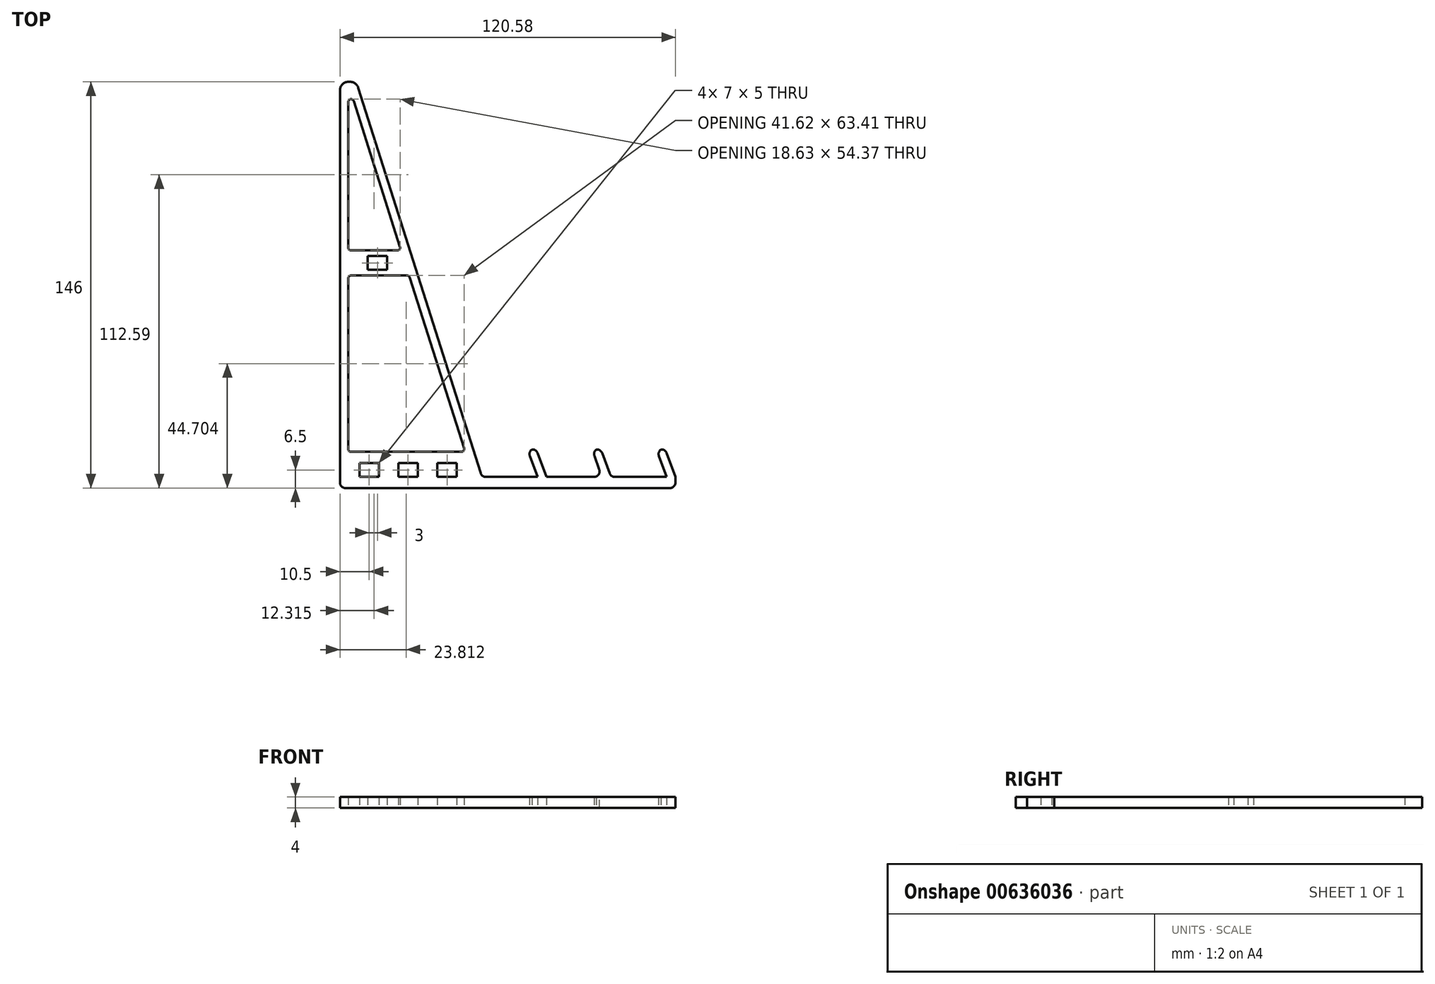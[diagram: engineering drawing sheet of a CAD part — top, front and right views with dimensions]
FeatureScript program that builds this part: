
annotation { "Feature Type Name" : "Feature", "Feature Type Description" : "" }
export const myFeature = defineFeature(function(context is Context, id is Id, definition is map)
    precondition{}
    {
        {
            var Q0;
            Q0=qCreatedBy(makeId("Top.planeOp"),FACE);
            var sketch = newSketch(context, id + "F0", { "sketchPlane" : qUnion([Q0])});
            skLineSegment(sketch, "E0", {"start": v(-51, -4) * mm, "end": v(-51, 139) * mm});
            skLineSegment(sketch, "E1.bottom", {"start": v(-44, 5) * mm, "end": v(-37, 5) * mm});
            skLineSegment(sketch, "E1.top", {"start": v(-44, 0) * mm, "end": v(-37, 0) * mm});
            skLineSegment(sketch, "E1.left", {"start": v(-44, 5) * mm, "end": v(-44, 0) * mm});
            skLineSegment(sketch, "E1.right", {"start": v(-37, 5) * mm, "end": v(-37, 0) * mm});
            skLineSegment(sketch, "E2", {"start": v(-44.43, 139.9) * mm, "end": v(0, 0) * mm});
            skLineSegment(sketch, "E3", {"start": v(-46.05, 135.09) * mm, "end": v(-29.41, 82.71) * mm});
            skLineSegment(sketch, "E4", {"start": v(-30.37, 81.4) * mm, "end": v(-47, 81.4) * mm});
            skLineSegment(sketch, "E5", {"start": v(-48, 82.4) * mm, "end": v(-48, 134.78) * mm});
            skLineSegment(sketch, "E6", {"start": v(-47, 9) * mm, "end": v(-7.37, 9) * mm});
            skLineSegment(sketch, "E7", {"start": v(-6.42, 10.3) * mm, "end": v(-25.92, 71.71) * mm});
            skLineSegment(sketch, "E8", {"start": v(-26.87, 72.4) * mm, "end": v(-47, 72.4) * mm});
            skLineSegment(sketch, "E9", {"start": v(-48, 71.4) * mm, "end": v(-48, 10) * mm});
            skPoint(sketch, "E10.visualSharp", {"position": v(-48, 141.24) * mm});
            skArc(sketch, "E10.filletArc", {"start": v(-46.05, 135.09) * mm, "mid": v(-47.15, 135.77) * mm, "end": v(-48, 134.78) * mm});
            skPoint(sketch, "E11.visualSharp", {"position": v(-48, 81.4) * mm});
            skArc(sketch, "E11.filletArc", {"start": v(-48, 82.4) * mm, "mid": v(-47.7, 81.7) * mm, "end": v(-47, 81.4) * mm});
            skPoint(sketch, "E12.visualSharp", {"position": v(-29, 81.4) * mm});
            skArc(sketch, "E12.filletArc", {"start": v(-30.37, 81.4) * mm, "mid": v(-29.56, 81.82) * mm, "end": v(-29.41, 82.71) * mm});
            skPoint(sketch, "E13.visualSharp", {"position": v(-26.14, 72.4) * mm});
            skArc(sketch, "E13.filletArc", {"start": v(-25.92, 71.71) * mm, "mid": v(-26.28, 72.21) * mm, "end": v(-26.87, 72.4) * mm});
            skPoint(sketch, "E14.visualSharp", {"position": v(-48, 72.4) * mm});
            skArc(sketch, "E14.filletArc", {"start": v(-47, 72.4) * mm, "mid": v(-47.7, 72.11) * mm, "end": v(-48, 71.4) * mm});
            skPoint(sketch, "E15.visualSharp", {"position": v(-48, 9) * mm});
            skArc(sketch, "E15.filletArc", {"start": v(-48, 10) * mm, "mid": v(-47.7, 9.3) * mm, "end": v(-47, 9) * mm});
            skPoint(sketch, "E16.visualSharp", {"position": v(-6, 9) * mm});
            skArc(sketch, "E16.filletArc", {"start": v(-7.37, 9) * mm, "mid": v(-6.57, 9.4) * mm, "end": v(-6.42, 10.3) * mm});
            skLineSegment(sketch, "E17.1.0.0", {"start": v(-30, 5) * mm, "end": v(-23, 5) * mm});
            skLineSegment(sketch, "E17.1.0.1", {"start": v(-23, 5) * mm, "end": v(-23, 0) * mm});
            skLineSegment(sketch, "E17.1.0.2", {"start": v(-30, 0) * mm, "end": v(-23, 0) * mm});
            skLineSegment(sketch, "E17.1.0.3", {"start": v(-30, 5) * mm, "end": v(-30, 0) * mm});
            skLineSegment(sketch, "E17.2.0.0", {"start": v(-16, 5) * mm, "end": v(-9, 5) * mm});
            skLineSegment(sketch, "E17.2.0.1", {"start": v(-9, 5) * mm, "end": v(-9, 0) * mm});
            skLineSegment(sketch, "E17.2.0.2", {"start": v(-16, 0) * mm, "end": v(-9, 0) * mm});
            skLineSegment(sketch, "E17.2.0.3", {"start": v(-16, 5) * mm, "end": v(-16, 0) * mm});
            skLineSegment(sketch, "E17.direction1", {"start": v(-44, 5) * mm, "end": v(-30, 5) * mm, "construction": true});
            skLineSegment(sketch, "E18.bottom", {"start": v(-41, 79.4) * mm, "end": v(-34, 79.4) * mm});
            skLineSegment(sketch, "E18.top", {"start": v(-41, 74.4) * mm, "end": v(-34, 74.4) * mm});
            skLineSegment(sketch, "E18.left", {"start": v(-41, 79.4) * mm, "end": v(-41, 74.4) * mm});
            skLineSegment(sketch, "E18.right", {"start": v(-34, 79.4) * mm, "end": v(-34, 74.4) * mm});
            skLineSegment(sketch, "E19", {"start": v(-48, 142) * mm, "end": v(-47.29, 142) * mm});
            skPoint(sketch, "E20.visualSharp", {"position": v(-45.1, 142) * mm});
            skArc(sketch, "E20.filletArc", {"start": v(-44.43, 139.9) * mm, "mid": v(-45.52, 141.42) * mm, "end": v(-47.29, 142) * mm});
            skPoint(sketch, "E21.visualSharp", {"position": v(-51, 142) * mm});
            skArc(sketch, "E21.filletArc", {"start": v(-48, 142) * mm, "mid": v(-50.12, 141.12) * mm, "end": v(-51, 139) * mm});
            skLineSegment(sketch, "E22", {"start": v(20, 0) * mm, "end": v(16.58, 9.4) * mm});
            skLineSegment(sketch, "E23", {"start": v(16.58, 9.4) * mm, "end": v(19.4, 10.42) * mm});
            skLineSegment(sketch, "E24", {"start": v(19.4, 10.42) * mm, "end": v(23.2, 0) * mm});
            skLineSegment(sketch, "E25", {"start": v(69.58, 0) * mm, "end": v(65.78, 10.42) * mm});
            skLineSegment(sketch, "E26", {"start": v(65.78, 10.42) * mm, "end": v(62.96, 9.4) * mm});
            skLineSegment(sketch, "E27", {"start": v(62.96, 9.4) * mm, "end": v(66.39, 0) * mm});
            skLineSegment(sketch, "E28", {"start": v(43.2, 0) * mm, "end": v(39.77, 9.4) * mm});
            skLineSegment(sketch, "E29", {"start": v(39.77, 9.4) * mm, "end": v(42.6, 10.42) * mm});
            skLineSegment(sketch, "E30", {"start": v(42.6, 10.42) * mm, "end": v(46.39, 0) * mm});
            skLineSegment(sketch, "E31", {"start": v(46.39, 0) * mm, "end": v(43.2, 0) * mm});
            skLineSegment(sketch, "E32", {"start": v(66.39, 0) * mm, "end": v(69.58, 0) * mm});
            skLineSegment(sketch, "E33", {"start": v(20, 0) * mm, "end": v(23.2, 0) * mm});
            skLineSegment(sketch, "E34", {"start": v(0, 0) * mm, "end": v(69.58, 0) * mm});
            skLineSegment(sketch, "E35", {"start": v(69.58, -4) * mm, "end": v(69.58, 0) * mm});
            skLineSegment(sketch, "E36", {"start": v(-51, -4) * mm, "end": v(69.58, -4) * mm});
            skSolve(sketch);
        }
        {
            var Q0;
            Q0=qSketchRegion(id+"F0",true);
            extrude(context, id + "F1", {"entities" : qUnion([Q0]), "depth" : 4 * mm, "offsetDistance" : 25 * mm});
        }
        {
            var Q0;
            Q0=makeQuery(id+"F1.opExtrude","SWEPT_EDGE",EDGE,{"disambiguationData":[OSD([sQuery(id+"F0.wireOp",EDGE,"gvBwSrxk-zvvE-uQVS-XaT0-VaHBcBpJHqCH"),sQuery(id+"F0.wireOp",EDGE,"E0")])]});
            var Q1;
            Q1=makeQuery(id+"F1.opExtrude","SWEPT_EDGE",EDGE,{"disambiguationData":[OSD([sQuery(id+"F0.wireOp",EDGE,"gvBwSrxk-zvvE-uQVS-XaT0-VaHBcBpJHqCH"),sQuery(id+"F0.wireOp",EDGE,"nh6h67nY-TW2N-W8gg-voCM-LFL465GMrIJx")])]});
            var Q2;
            Q2=makeQuery(id+"F1.opExtrude","SWEPT_EDGE",EDGE,{"disambiguationData":[OSD([sQuery(id+"F0.wireOp",EDGE,"nh6h67nY-TW2N-W8gg-voCM-LFL465GMrIJx"),sQuery(id+"F0.wireOp",EDGE,"E25"),sQuery(id+"F0.wireOp",EDGE,"9GKQQmJT-vaMx-PueB-U0vb-JAIJfWlyNM5I")])]});
            var Q3;
            Q3=makeQuery(id+"F1.opExtrude","SWEPT_EDGE",EDGE,{"disambiguationData":[OSD([sQuery(id+"F0.wireOp",EDGE,"E25"),sQuery(id+"F0.wireOp",EDGE,"E26")])]});
            var Q4;
            Q4=makeQuery(id+"F1.opExtrude","SWEPT_EDGE",EDGE,{"disambiguationData":[OSD([sQuery(id+"F0.wireOp",EDGE,"E26"),sQuery(id+"F0.wireOp",EDGE,"E27")])]});
            var Q5;
            Q5=makeQuery(id+"F1.opExtrude","SWEPT_EDGE",EDGE,{"disambiguationData":[OSD([sQuery(id+"F0.wireOp",EDGE,"UcYIQvCT-M2cl-KZQb-FalE-3mOYIRNoCB6S"),sQuery(id+"F0.wireOp",EDGE,"E27"),sQuery(id+"F0.wireOp",EDGE,"9GKQQmJT-vaMx-PueB-U0vb-JAIJfWlyNM5I")])]});
            var Q6;
            Q6=makeQuery(id+"F1.opExtrude","SWEPT_EDGE",EDGE,{"disambiguationData":[OSD([sQuery(id+"F0.wireOp",EDGE,"E24"),sQuery(id+"F0.wireOp",EDGE,"UcYIQvCT-M2cl-KZQb-FalE-3mOYIRNoCB6S")])]});
            var Q7;
            Q7=makeQuery(id+"F1.opExtrude","SWEPT_EDGE",EDGE,{"disambiguationData":[OSD([sQuery(id+"F0.wireOp",EDGE,"E23"),sQuery(id+"F0.wireOp",EDGE,"E24")])]});
            var Q8;
            Q8=makeQuery(id+"F1.opExtrude","SWEPT_EDGE",EDGE,{"disambiguationData":[OSD([sQuery(id+"F0.wireOp",EDGE,"E22"),sQuery(id+"F0.wireOp",EDGE,"E23")])]});
            var Q9;
            Q9=makeQuery(id+"F1.opExtrude","SWEPT_EDGE",EDGE,{"disambiguationData":[OSD([sQuery(id+"F0.wireOp",EDGE,"E22"),sQuery(id+"F0.wireOp",EDGE,"UcYIQvCT-M2cl-KZQb-FalE-3mOYIRNoCB6S")])]});
            var Q10;
            Q10=makeQuery(id+"F1.opExtrude","SWEPT_EDGE",EDGE,{"disambiguationData":[OSD([sQuery(id+"F0.wireOp",EDGE,"E2"),sQuery(id+"F0.wireOp",EDGE,"UcYIQvCT-M2cl-KZQb-FalE-3mOYIRNoCB6S")])]});
            var Q11;
            Q11=makeQuery(id+"F1.opExtrude","SWEPT_EDGE",EDGE,{"disambiguationData":[OSD([sQuery(id+"F0.wireOp",EDGE,"E28"),sQuery(id+"F0.wireOp",EDGE,"E29")])]});
            var Q12;
            Q12=makeQuery(id+"F1.opExtrude","SWEPT_EDGE",EDGE,{"disambiguationData":[OSD([sQuery(id+"F0.wireOp",EDGE,"E29"),sQuery(id+"F0.wireOp",EDGE,"E30")])]});
            var Q13;
            Q13=makeQuery(id+"F1.opExtrude","SWEPT_EDGE",EDGE,{"disambiguationData":[OSD([sQuery(id+"F0.wireOp",EDGE,"UcYIQvCT-M2cl-KZQb-FalE-3mOYIRNoCB6S"),sQuery(id+"F0.wireOp",EDGE,"E28"),sQuery(id+"F0.wireOp",EDGE,"E31")])]});
            var Q14;
            Q14=makeQuery(id+"F1.opExtrude","SWEPT_EDGE",EDGE,{"disambiguationData":[OSD([sQuery(id+"F0.wireOp",EDGE,"UcYIQvCT-M2cl-KZQb-FalE-3mOYIRNoCB6S"),sQuery(id+"F0.wireOp",EDGE,"E30"),sQuery(id+"F0.wireOp",EDGE,"E31")])]});
            var Q15;
            Q15=makeQuery(id+"F1.opExtrude","SWEPT_EDGE",EDGE,{"disambiguationData":[OSD([sQuery(id+"F0.wireOp",EDGE,"E35"),sQuery(id+"F0.wireOp",EDGE,"E36")])]});
            fillet(context, id + "F2", {"entities" : qUnion([Q0, Q1, Q2, Q3, Q4, Q5, Q6, Q7, Q8, Q9, Q10, Q11, Q12, Q13, Q14, Q15]), "radius" : 2 * mm, "tangentPropagation" : true, "allowEdgeOverflow" : false});
        }
    });
